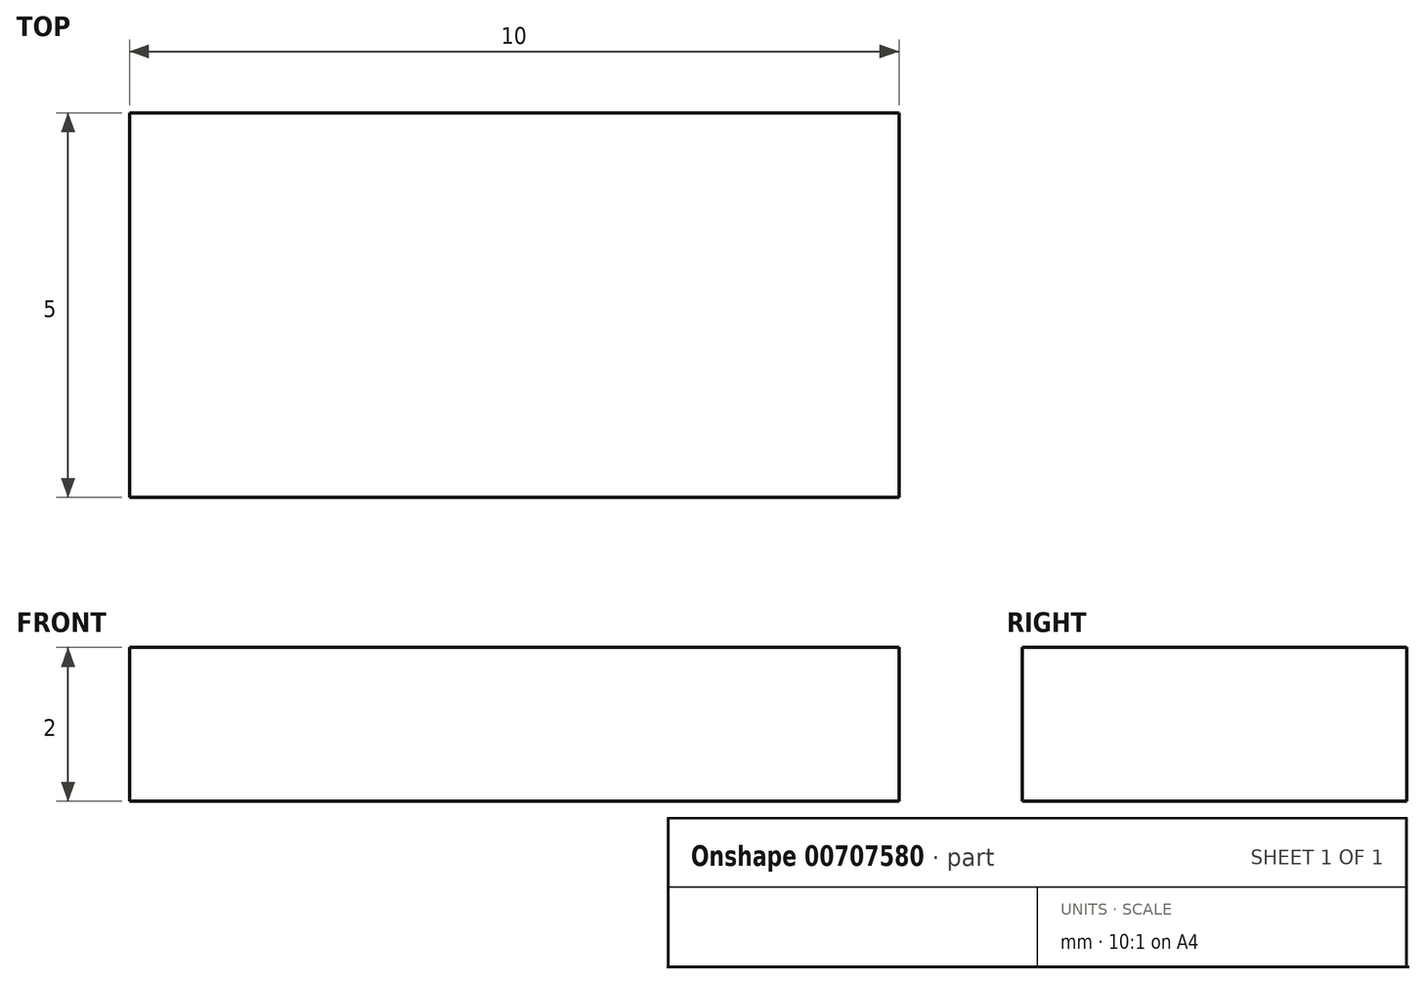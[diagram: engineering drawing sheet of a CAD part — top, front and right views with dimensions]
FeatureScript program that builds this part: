
annotation { "Feature Type Name" : "Feature", "Feature Type Description" : "" }
export const myFeature = defineFeature(function(context is Context, id is Id, definition is map)
    precondition{}
    {
        {
            var Q0;
            Q0=qCreatedBy(makeId("Top.planeOp"),FACE);
            var sketch = newSketch(context, id + "F0", { "sketchPlane" : qUnion([Q0])});
            skLineSegment(sketch, "E0.bottom", {"start": v(-5, 2.5) * mm, "end": v(5, 2.5) * mm});
            skLineSegment(sketch, "E0.top", {"start": v(-5, -2.5) * mm, "end": v(5, -2.5) * mm});
            skLineSegment(sketch, "E0.left", {"start": v(-5, 2.5) * mm, "end": v(-5, -2.5) * mm});
            skLineSegment(sketch, "E0.right", {"start": v(5, 2.5) * mm, "end": v(5, -2.5) * mm});
            skPoint(sketch, "E0.middle", {"position": v(0, 0) * mm});
            skSolve(sketch);
        }
        {
            var Q0;
            Q0=makeQuery(id+"F0.imprint","IMPRINT",FACE,{"disambiguationData":[TD([[makeQuery(id+"F0.imprint","IMPRINT",EDGE,{"derivedFrom":sQuery(id+"F0.wireOp",EDGE,"E0.bottom")}),-1.0]])]});
            extrude(context, id + "F1", {"entities" : qUnion([Q0]), "depth" : 2 * mm, "offsetDistance" : 25 * mm});
        }
    });
